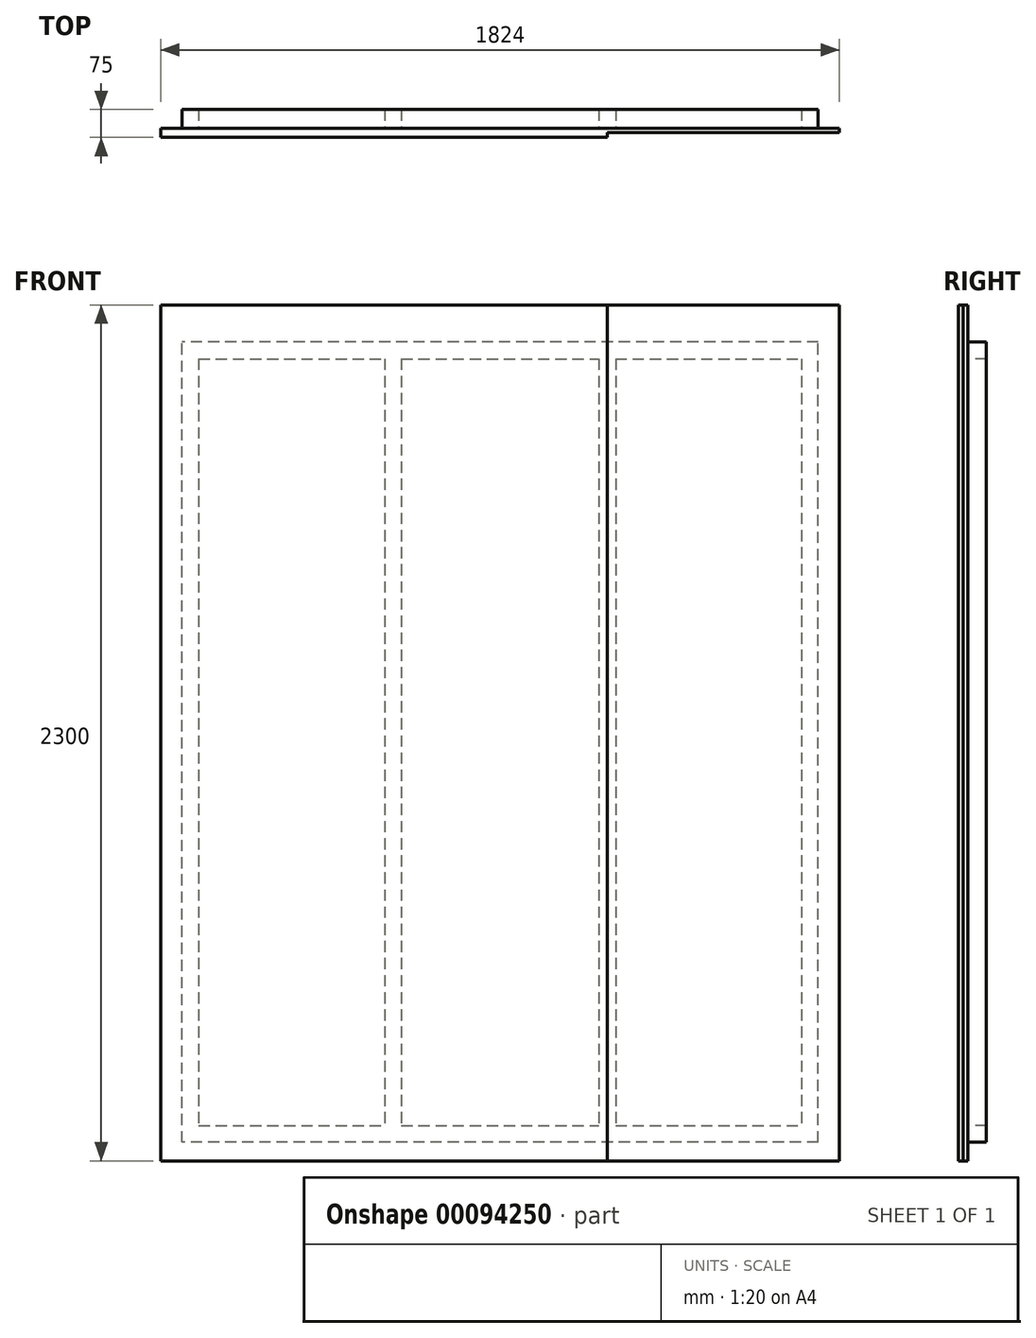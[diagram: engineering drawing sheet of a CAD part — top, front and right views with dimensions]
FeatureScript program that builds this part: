
annotation { "Feature Type Name" : "Feature", "Feature Type Description" : "" }
export const myFeature = defineFeature(function(context is Context, id is Id, definition is map)
    precondition{}
    {
        {
            var Q0;
            Q0=qCreatedBy(makeId("Front.planeOp"),FACE);
            var sketch = newSketch(context, id + "F0", { "sketchPlane" : qUnion([Q0])});
            skLineSegment(sketch, "E0.bottom", {"start": v(855, -1075) * mm, "end": v(-855, -1075) * mm});
            skLineSegment(sketch, "E0.top", {"start": v(855, 1075) * mm, "end": v(-855, 1075) * mm});
            skLineSegment(sketch, "E0.left", {"start": v(855, -1075) * mm, "end": v(855, 1075) * mm});
            skLineSegment(sketch, "E0.right", {"start": v(-855, -1075) * mm, "end": v(-855, 1075) * mm});
            skPoint(sketch, "E0.middle", {"position": v(0, 0) * mm});
            skLineSegment(sketch, "E1", {"start": v(-855, -1030) * mm, "end": v(855, -1030) * mm});
            skLineSegment(sketch, "E2", {"start": v(-855, 1030) * mm, "end": v(855, 1030) * mm});
            skLineSegment(sketch, "E3", {"start": v(-810, 1030) * mm, "end": v(-810, -1030) * mm});
            skLineSegment(sketch, "E4", {"start": v(-310.5, 1030) * mm, "end": v(-310.5, -1030) * mm});
            skLineSegment(sketch, "E5", {"start": v(-1110.96, 0) * mm, "end": v(1267.85, 0) * mm, "construction": true});
            skLineSegment(sketch, "E6", {"start": v(0, 1506.41) * mm, "end": v(0, -1337.08) * mm, "construction": true});
            skLineSegment(sketch, "E7", {"start": v(-288, 1424.82) * mm, "end": v(-288, -1205.47) * mm, "construction": true});
            skLineSegment(sketch, "E8.MirrorCS", {"start": v(288, 1424.82) * mm, "end": v(288, -1205.47) * mm, "construction": true});
            skLineSegment(sketch, "E9.MirrorCS", {"start": v(-265.5, 1030) * mm, "end": v(-265.5, -1030) * mm});
            skLineSegment(sketch, "E10.MirrorCS", {"start": v(265.5, 1030) * mm, "end": v(265.5, -1030) * mm});
            skLineSegment(sketch, "E11.MirrorCS", {"start": v(310.5, 1030) * mm, "end": v(310.5, -1030) * mm});
            skLineSegment(sketch, "E12.MirrorCS", {"start": v(810, 1030) * mm, "end": v(810, -1030) * mm});
            skLineSegment(sketch, "E13.bottom", {"start": v(-912, 1175) * mm, "end": v(912, 1175) * mm});
            skLineSegment(sketch, "E13.top", {"start": v(-912, -1125) * mm, "end": v(912, -1125) * mm});
            skLineSegment(sketch, "E13.left", {"start": v(-912, 1175) * mm, "end": v(-912, -1125) * mm});
            skLineSegment(sketch, "E13.right", {"start": v(912, 1175) * mm, "end": v(912, -1125) * mm});
            skLineSegment(sketch, "E14", {"start": v(288, 1175) * mm, "end": v(288, -1125) * mm});
            skSolve(sketch);
        }
        {
            var Q0;
            {var subQ1=sQuery(id+"F0.wireOp",EDGE,"E0.left");var subQ7=sQuery(id+"F0.wireOp",EDGE,"E1");var subQ8=makeQuery(id+"F0.imprint","INTERSECT",VERTEX,{"derivedFrom":[subQ1,subQ7]});Q0=makeQuery(id+"F0.imprint","IMPRINT",FACE,{"disambiguationData":[TD([[makeQuery(id+"F0.imprint","IMPRINT",EDGE,{"disambiguationData":[TD([[subQ8,-1.0]])],"derivedFrom":subQ1}),1.0]])]});}
            var Q1;
            {var subQ4=sQuery(id+"F0.wireOp",EDGE,"E0.bottom");Q1=makeQuery(id+"F0.imprint","IMPRINT",FACE,{"disambiguationData":[TD([[makeQuery(id+"F0.imprint","IMPRINT",EDGE,{"derivedFrom":subQ4}),-1.0]])]});}
            var Q2;
            {var subQ1=sQuery(id+"F0.wireOp",EDGE,"E0.right");var subQ5=sQuery(id+"F0.wireOp",EDGE,"E1");var subQ6=makeQuery(id+"F0.imprint","INTERSECT",VERTEX,{"derivedFrom":[subQ1,subQ5]});Q2=makeQuery(id+"F0.imprint","IMPRINT",FACE,{"disambiguationData":[TD([[makeQuery(id+"F0.imprint","IMPRINT",EDGE,{"disambiguationData":[TD([[subQ6,-1.0]])],"derivedFrom":subQ1}),-1.0]])]});}
            var Q3;
            {var subQ0=sQuery(id+"F0.wireOp",EDGE,"4UqkaRAp-bFaK-UsER-9ZWJ-XKRwch9azS2F");Q3=makeQuery(id+"F0.imprint","IMPRINT",FACE,{"disambiguationData":[TD([[makeQuery(id+"F0.imprint","IMPRINT",EDGE,{"derivedFrom":subQ0}),1.0]])]});}
            var Q4;
            {var subQ4=sQuery(id+"F0.wireOp",EDGE,"Y9YJFoT9-6JT1-CQLA-tPWW-gQWgdt1ssLVv");Q4=makeQuery(id+"F0.imprint","IMPRINT",FACE,{"disambiguationData":[TD([[makeQuery(id+"F0.imprint","IMPRINT",EDGE,{"derivedFrom":subQ4}),-1.0]])]});}
            var Q5;
            {var subQ0=sQuery(id+"F0.wireOp",EDGE,"E10.MirrorCS");var subQ3=sQuery(id+"F0.wireOp",EDGE,"E1");var subQ4=makeQuery(id+"F0.imprint","INTERSECT",VERTEX,{"derivedFrom":[subQ3,subQ0]});Q5=makeQuery(id+"F0.imprint","IMPRINT",FACE,{"disambiguationData":[TD([[makeQuery(id+"F0.imprint","IMPRINT",EDGE,{"disambiguationData":[TD([[subQ4,-1.0]])],"derivedFrom":subQ3}),1.0]])]});}
            var Q6;
            {var subQ0=sQuery(id+"F0.wireOp",EDGE,"a5246e65-98c1-44be-81f6-b830822bc63a0.MirrorCS");Q6=makeQuery(id+"F0.imprint","IMPRINT",FACE,{"disambiguationData":[TD([[makeQuery(id+"F0.imprint","IMPRINT",EDGE,{"derivedFrom":subQ0}),1.0]])]});}
            var Q7;
            {var subQ4=sQuery(id+"F0.wireOp",EDGE,"E0.top");Q7=makeQuery(id+"F0.imprint","IMPRINT",FACE,{"disambiguationData":[TD([[makeQuery(id+"F0.imprint","IMPRINT",EDGE,{"derivedFrom":subQ4}),1.0]])]});}
            var Q8;
            {var subQ0=sQuery(id+"F0.wireOp",EDGE,"E4");var subQ7=sQuery(id+"F0.wireOp",EDGE,"E1");var subQ8=makeQuery(id+"F0.imprint","INTERSECT",VERTEX,{"derivedFrom":[subQ7,subQ0]});Q8=makeQuery(id+"F0.imprint","IMPRINT",FACE,{"disambiguationData":[TD([[makeQuery(id+"F0.imprint","IMPRINT",EDGE,{"disambiguationData":[TD([[subQ8,-1.0]])],"derivedFrom":subQ7}),1.0]])]});}
            var Q9;
            {var subQ3=sQuery(id+"F0.wireOp",EDGE,"E13.top");var subQ4=sQuery(id+"F0.wireOp",EDGE,"E0.left");var subQ5=makeQuery(id+"F0.imprint","INTERSECT",VERTEX,{"derivedFrom":[subQ4,subQ3]});Q9=makeQuery(id+"F0.imprint","IMPRINT",FACE,{"disambiguationData":[TD([[makeQuery(id+"F0.imprint","IMPRINT",EDGE,{"disambiguationData":[TD([[subQ5,-1.0]])],"derivedFrom":subQ4}),1.0]])]});}
            var Q10;
            {var subQ3=sQuery(id+"F0.wireOp",EDGE,"E0.right");var subQ4=sQuery(id+"F0.wireOp",EDGE,"E0.top");var subQ5=makeQuery(id+"F0.imprint","INTERSECT",VERTEX,{"derivedFrom":[subQ4,subQ3]});Q10=makeQuery(id+"F0.imprint","IMPRINT",FACE,{"disambiguationData":[TD([[makeQuery(id+"F0.imprint","IMPRINT",EDGE,{"disambiguationData":[TD([[subQ5,1.0]])],"derivedFrom":subQ4}),1.0]])]});}
            var Q11;
            {var subQ0=sQuery(id+"F0.wireOp",EDGE,"E11.MirrorCS");Q11=makeQuery(id+"F0.imprint","IMPRINT",FACE,{"disambiguationData":[TD([[makeQuery(id+"F0.imprint","IMPRINT",EDGE,{"derivedFrom":subQ0}),-1.0]])]});}
            var Q12;
            {var subQ3=sQuery(id+"F0.wireOp",EDGE,"E0.right");var subQ6=sQuery(id+"F0.wireOp",EDGE,"E0.bottom");var subQ9=makeQuery(id+"F0.imprint","INTERSECT",VERTEX,{"derivedFrom":[subQ6,subQ3]});Q12=makeQuery(id+"F0.imprint","IMPRINT",FACE,{"disambiguationData":[TD([[makeQuery(id+"F0.imprint","IMPRINT",EDGE,{"disambiguationData":[TD([[subQ9,1.0]])],"derivedFrom":subQ6}),-1.0]])]});}
            extrude(context, id + "F1", {"entities" : qUnion([Q0, Q1, Q2, Q3, Q4, Q5, Q6, Q7, Q8, Q9, Q10, Q11, Q12]), "oppositeDirection" : true, "depth" : 50 * mm});
        }
        {
            var Q0;
            {var subQ5=sQuery(id+"F0.wireOp",EDGE,"E13.right");Q0=makeQuery(id+"F0.imprint","IMPRINT",FACE,{"disambiguationData":[TD([[makeQuery(id+"F0.imprint","IMPRINT",EDGE,{"derivedFrom":subQ5}),-1.0]])]});}
            var Q1;
            {var subQ0=sQuery(id+"F0.wireOp",EDGE,"E11.MirrorCS");Q1=makeQuery(id+"F0.imprint","IMPRINT",FACE,{"disambiguationData":[TD([[makeQuery(id+"F0.imprint","IMPRINT",EDGE,{"derivedFrom":subQ0}),1.0]])]});}
            var Q2;
            {var subQ4=sQuery(id+"F0.wireOp",EDGE,"E0.left");var subQ5=sQuery(id+"F0.wireOp",EDGE,"E0.bottom");var subQ6=makeQuery(id+"F0.imprint","INTERSECT",VERTEX,{"derivedFrom":[subQ5,subQ4]});Q2=makeQuery(id+"F0.imprint","IMPRINT",FACE,{"disambiguationData":[TD([[makeQuery(id+"F0.imprint","IMPRINT",EDGE,{"disambiguationData":[TD([[subQ6,-1.0]])],"derivedFrom":subQ5}),-1.0]])]});}
            var Q3;
            {var subQ5=sQuery(id+"F0.wireOp",EDGE,"E12.MirrorCS");Q3=makeQuery(id+"F0.imprint","IMPRINT",FACE,{"disambiguationData":[TD([[makeQuery(id+"F0.imprint","IMPRINT",EDGE,{"derivedFrom":subQ5}),1.0]])]});}
            var Q4;
            {var subQ3=sQuery(id+"F0.wireOp",EDGE,"E0.left");var subQ4=sQuery(id+"F0.wireOp",EDGE,"E0.top");var subQ5=makeQuery(id+"F0.imprint","INTERSECT",VERTEX,{"derivedFrom":[subQ4,subQ3]});Q4=makeQuery(id+"F0.imprint","IMPRINT",FACE,{"disambiguationData":[TD([[makeQuery(id+"F0.imprint","IMPRINT",EDGE,{"disambiguationData":[TD([[subQ5,-1.0]])],"derivedFrom":subQ4}),1.0]])]});}
            var Q5;
            {var subQ0=sQuery(id+"F0.wireOp",EDGE,"E11.MirrorCS");Q5=makeQuery(id+"F0.imprint","IMPRINT",FACE,{"disambiguationData":[TD([[makeQuery(id+"F0.imprint","IMPRINT",EDGE,{"derivedFrom":subQ0}),-1.0]])]});}
            extrude(context, id + "F2", {"entities" : qUnion([Q0, Q1, Q2, Q3, Q4, Q5]), "operationType" : NewBodyOperationType.ADD, "depth" : 12 * mm});
        }
        {
            var Q0;
            {var subQ7=sQuery(id+"F0.wireOp",EDGE,"E13.left");Q0=makeQuery(id+"F0.imprint","IMPRINT",FACE,{"disambiguationData":[TD([[makeQuery(id+"F0.imprint","IMPRINT",EDGE,{"derivedFrom":subQ7}),1.0]])]});}
            var Q1;
            {var subQ0=sQuery(id+"F0.wireOp",EDGE,"E4");Q1=makeQuery(id+"F0.imprint","IMPRINT",FACE,{"disambiguationData":[TD([[makeQuery(id+"F0.imprint","IMPRINT",EDGE,{"derivedFrom":subQ0}),1.0]])]});}
            var Q2;
            {var subQ3=sQuery(id+"F0.wireOp",EDGE,"E0.right");var subQ4=sQuery(id+"F0.wireOp",EDGE,"E0.top");var subQ5=makeQuery(id+"F0.imprint","INTERSECT",VERTEX,{"derivedFrom":[subQ4,subQ3]});Q2=makeQuery(id+"F0.imprint","IMPRINT",FACE,{"disambiguationData":[TD([[makeQuery(id+"F0.imprint","IMPRINT",EDGE,{"disambiguationData":[TD([[subQ5,1.0]])],"derivedFrom":subQ4}),1.0]])]});}
            var Q3;
            {var subQ5=sQuery(id+"F0.wireOp",EDGE,"E3");Q3=makeQuery(id+"F0.imprint","IMPRINT",FACE,{"disambiguationData":[TD([[makeQuery(id+"F0.imprint","IMPRINT",EDGE,{"derivedFrom":subQ5}),-1.0]])]});}
            var Q4;
            {var subQ0=sQuery(id+"F0.wireOp",EDGE,"E3");Q4=makeQuery(id+"F0.imprint","IMPRINT",FACE,{"disambiguationData":[TD([[makeQuery(id+"F0.imprint","IMPRINT",EDGE,{"derivedFrom":subQ0}),1.0]])]});}
            var Q5;
            {var subQ0=sQuery(id+"F0.wireOp",EDGE,"E9.MirrorCS");Q5=makeQuery(id+"F0.imprint","IMPRINT",FACE,{"disambiguationData":[TD([[makeQuery(id+"F0.imprint","IMPRINT",EDGE,{"derivedFrom":subQ0}),1.0]])]});}
            var Q6;
            {var subQ3=sQuery(id+"F0.wireOp",EDGE,"E0.right");var subQ6=sQuery(id+"F0.wireOp",EDGE,"E0.bottom");var subQ9=makeQuery(id+"F0.imprint","INTERSECT",VERTEX,{"derivedFrom":[subQ6,subQ3]});Q6=makeQuery(id+"F0.imprint","IMPRINT",FACE,{"disambiguationData":[TD([[makeQuery(id+"F0.imprint","IMPRINT",EDGE,{"disambiguationData":[TD([[subQ9,1.0]])],"derivedFrom":subQ6}),-1.0]])]});}
            var Q7;
            {var subQ0=sQuery(id+"F0.wireOp",EDGE,"E10.MirrorCS");Q7=makeQuery(id+"F0.imprint","IMPRINT",FACE,{"disambiguationData":[TD([[makeQuery(id+"F0.imprint","IMPRINT",EDGE,{"derivedFrom":subQ0}),1.0]])]});}
            extrude(context, id + "F3", {"entities" : qUnion([Q0, Q1, Q2, Q3, Q4, Q5, Q6, Q7]), "operationType" : NewBodyOperationType.ADD, "depth" : 25 * mm});
        }
    });
